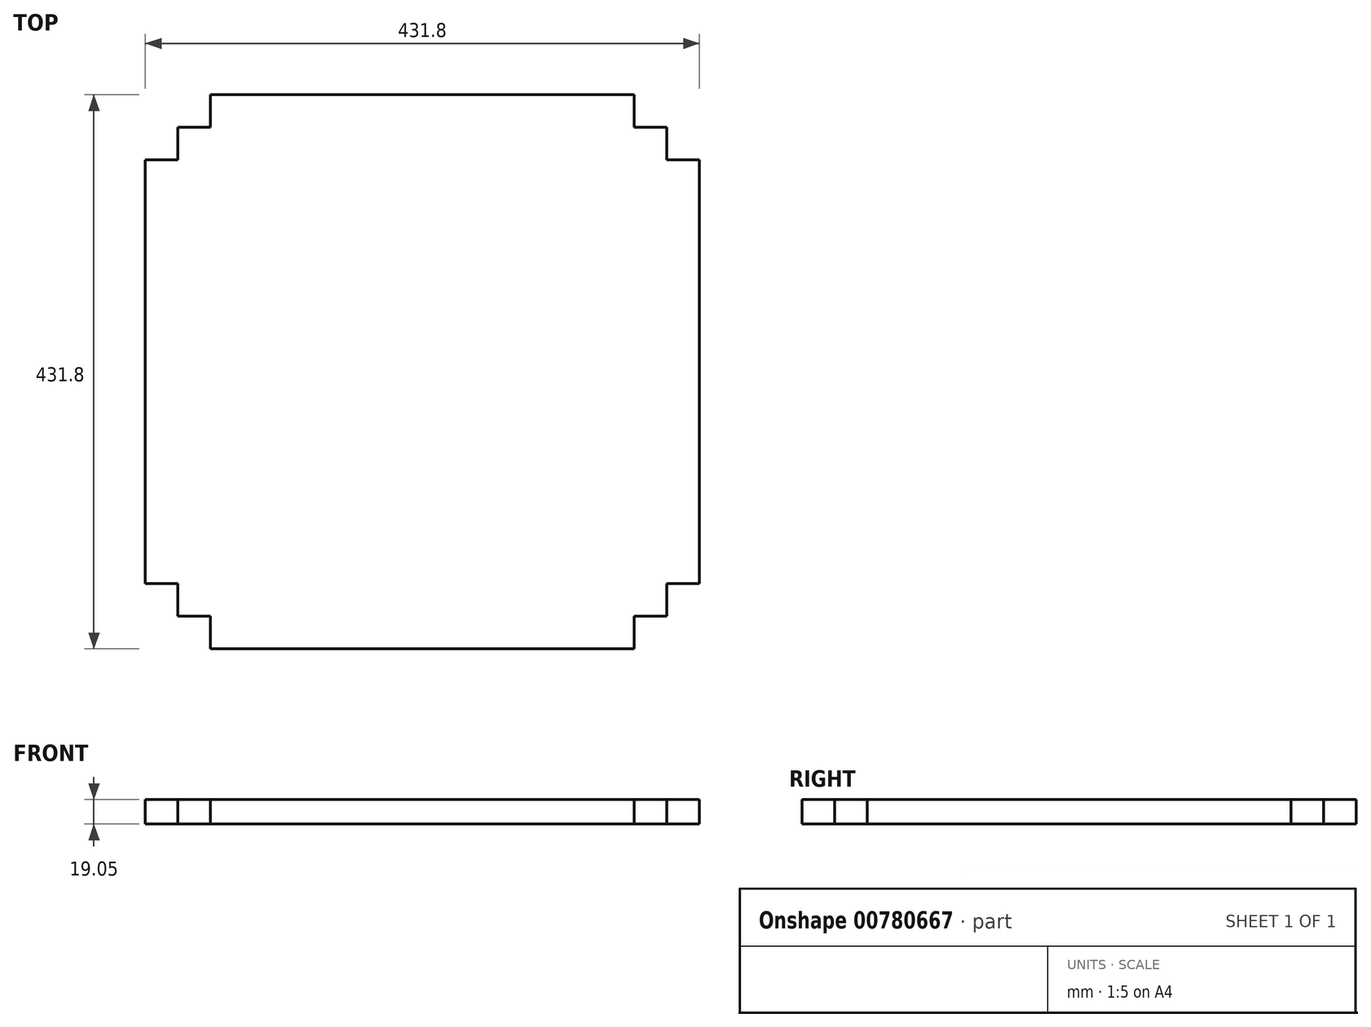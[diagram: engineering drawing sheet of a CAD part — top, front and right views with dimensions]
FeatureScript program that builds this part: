
annotation { "Feature Type Name" : "Feature", "Feature Type Description" : "" }
export const myFeature = defineFeature(function(context is Context, id is Id, definition is map)
    precondition{}
    {
        {
            var Q0;
            Q0=qCreatedBy(makeId("Top.planeOp"),FACE);
            var sketch = newSketch(context, id + "F0", { "sketchPlane" : qUnion([Q0])});
            skLineSegment(sketch, "E0", {"start": v(-49.26, 109.53) * mm, "end": v(-23.86, 109.53) * mm});
            skLineSegment(sketch, "E1", {"start": v(-23.86, 109.53) * mm, "end": v(-23.86, 134.93) * mm});
            skLineSegment(sketch, "E2", {"start": v(-23.86, 134.93) * mm, "end": v(1.54, 134.93) * mm});
            skLineSegment(sketch, "E3", {"start": v(1.54, 134.93) * mm, "end": v(1.54, 160.33) * mm});
            skLineSegment(sketch, "E4", {"start": v(1.54, 160.33) * mm, "end": v(331.74, 160.33) * mm});
            skLineSegment(sketch, "E5", {"start": v(331.74, 160.33) * mm, "end": v(331.74, 134.93) * mm});
            skLineSegment(sketch, "E6", {"start": v(331.74, 134.93) * mm, "end": v(357.14, 134.93) * mm});
            skLineSegment(sketch, "E7", {"start": v(357.14, 134.93) * mm, "end": v(357.14, 109.53) * mm});
            skLineSegment(sketch, "E8", {"start": v(357.14, 109.53) * mm, "end": v(382.54, 109.53) * mm});
            skLineSegment(sketch, "E9", {"start": v(382.54, 109.53) * mm, "end": v(382.54, -220.67) * mm});
            skLineSegment(sketch, "E10", {"start": v(382.54, -220.67) * mm, "end": v(357.14, -220.67) * mm});
            skLineSegment(sketch, "E11", {"start": v(357.14, -220.67) * mm, "end": v(357.14, -246.07) * mm});
            skLineSegment(sketch, "E12", {"start": v(357.14, -246.07) * mm, "end": v(331.74, -246.07) * mm});
            skLineSegment(sketch, "E13", {"start": v(331.74, -246.07) * mm, "end": v(331.74, -271.47) * mm});
            skLineSegment(sketch, "E14", {"start": v(331.74, -271.47) * mm, "end": v(1.54, -271.47) * mm});
            skLineSegment(sketch, "E15", {"start": v(1.54, -271.47) * mm, "end": v(1.54, -246.07) * mm});
            skLineSegment(sketch, "E16", {"start": v(1.54, -246.07) * mm, "end": v(-23.86, -246.07) * mm});
            skLineSegment(sketch, "E17", {"start": v(-23.86, -246.07) * mm, "end": v(-23.86, -220.67) * mm});
            skLineSegment(sketch, "E18", {"start": v(-23.86, -220.67) * mm, "end": v(-49.26, -220.67) * mm});
            skLineSegment(sketch, "E19", {"start": v(-49.26, 109.53) * mm, "end": v(-49.26, -220.67) * mm});
            skSolve(sketch);
        }
        {
            var Q0;
            Q0=makeQuery(id+"F0.imprint","IMPRINT",FACE,{"disambiguationData":[TD([[makeQuery(id+"F0.imprint","IMPRINT",EDGE,{"derivedFrom":sQuery(id+"F0.wireOp",EDGE,"E0")}),-1.0]])]});
            extrude(context, id + "F1", {"entities" : qUnion([Q0]), "depth" : 19.05 * mm, "offsetDistance" : 25.4 * mm});
        }
    });
